# Revit family: WIA
name_source: partatom
category: Plumbing Fixtures
revit_build: Autodesk Revit Architecture 2015 (Build: 20140606_1530(x64)
units: mm (PartAtom-declared; Revit-internal decimal feet)

## types (10) — shared parameters
Glass = Glass
Manufacturer = SanSwiss
Metal = Aluminum - Polished
Model = WIA
Outlet pipe nominal diameter = 50 mm
Type Comments = ILA
URL = www.sanswiss.com
Water flow rate = 0.6 L/s
zero-valued in all types: Number of elements

## per-type parameters (varying)
| type | A | B | Shower base |
| 900x900 | 900 mm  [stored 2.95276 ft] | 900 mm  [stored 2.95276 ft] | shower base : 900x900 |
| 800x900 | 800 mm  [stored 2.62467 ft] | 900 mm  [stored 2.95276 ft] | shower base : 800x900 |
| 800x1200 | 800 mm  [stored 2.62467 ft] | 1200 mm | shower base : 800x1200 |
| 800x1000 | 800 mm  [stored 2.62467 ft] | 1000 mm  [stored 3.28084 ft] | shower base : 800x1000 |
| 900x1400 | 900 mm  [stored 2.95276 ft] | 1400 mm  [stored 4.59318 ft] | shower base : 900x1400 |
| 900x1200 | 900 mm  [stored 2.95276 ft] | 1200 mm | shower base : 900x1200 |
| 900x1000 | 900 mm  [stored 2.95276 ft] | 1000 mm  [stored 3.28084 ft] | shower base : 900x1000 |
| 900x1600 | 900 mm  [stored 2.95276 ft] | 1600 mm  [stored 5.24934 ft] | shower base : 900x1600 |
| 900x800 | 900 mm  [stored 2.95276 ft] | 800 mm  [stored 2.62467 ft] | shower base : 900x800 |
| 900x1500 | 900 mm  [stored 2.95276 ft] | 1500 mm  [stored 4.92126 ft] | shower base : 900x1500 |

note: [stored X ft] marks values corroborated as IEEE doubles in the binary element streams (Revit-internal decimal feet)

## geometry (parser evidence)
native form markers: Sweep x17
no freeform markers — native parametric forms only
